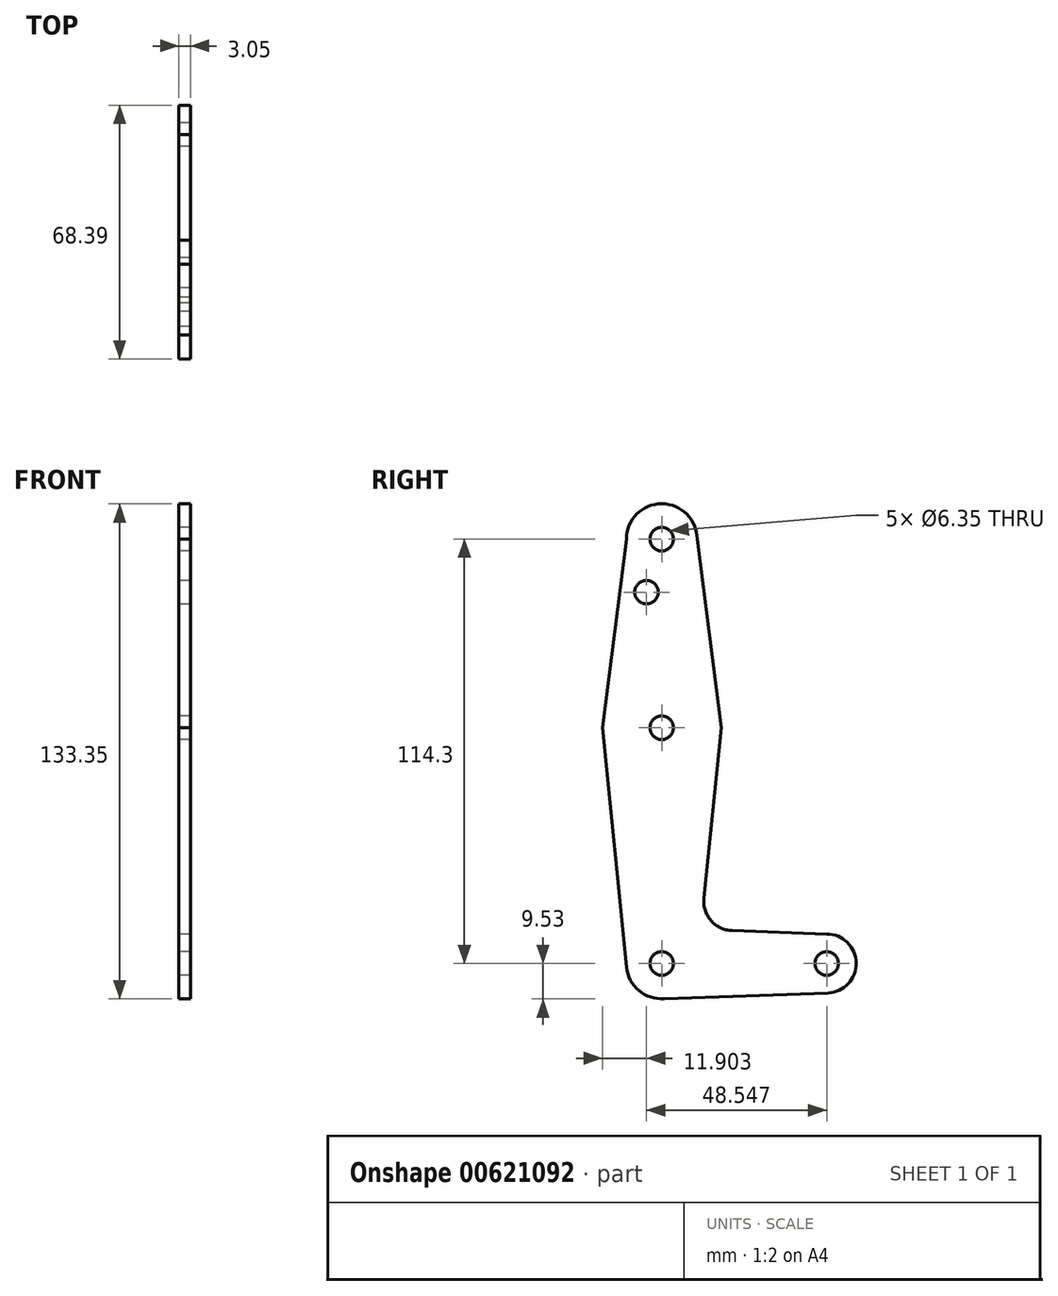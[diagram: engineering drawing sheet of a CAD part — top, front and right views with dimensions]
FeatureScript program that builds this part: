
annotation { "Feature Type Name" : "Feature", "Feature Type Description" : "" }
export const myFeature = defineFeature(function(context is Context, id is Id, definition is map)
    precondition{}
    {
        {
            var Q0;
            Q0=qCreatedBy(makeId("Right.planeOp"),FACE);
            var sketch = newSketch(context, id + "F0", { "sketchPlane" : qUnion([Q0])});
            skLineSegment(sketch, "E0", {"start": v(0, 0) * mm, "end": v(0, 50.8) * mm});
            skLineSegment(sketch, "E1", {"start": v(0, 50.8) * mm, "end": v(0, 0) * mm});
            skLineSegment(sketch, "E2", {"start": v(0, -63.5) * mm, "end": v(0, 0) * mm});
            skLineSegment(sketch, "E3", {"start": v(0, -63.5) * mm, "end": v(44.45, -63.5) * mm});
            skCircle(sketch, "E4", {"center": v(0, 0) * mm, "radius": 15.88 * mm});
            skCircle(sketch, "E5", {"center": v(0, 50.8) * mm, "radius": 9.53 * mm});
            skCircle(sketch, "E6", {"center": v(0, -63.5) * mm, "radius": 9.53 * mm});
            skCircle(sketch, "E7", {"center": v(44.45, -63.5) * mm, "radius": 7.94 * mm});
            skLineSegment(sketch, "E8", {"start": v(9.52, 50.8) * mm, "end": v(16, 0) * mm});
            skLineSegment(sketch, "E9", {"start": v(-9.52, 50.8) * mm, "end": v(-16, 0) * mm});
            skLineSegment(sketch, "E10", {"start": v(-16, 0) * mm, "end": v(-9.53, 50.8) * mm});
            skLineSegment(sketch, "E11", {"start": v(16, 0) * mm, "end": v(11.36, -45.9) * mm});
            skLineSegment(sketch, "E12", {"start": v(-16, 0) * mm, "end": v(-9.48, -64.46) * mm});
            skLineSegment(sketch, "E13", {"start": v(44.45, -55.56) * mm, "end": v(18.98, -54.65) * mm});
            skLineSegment(sketch, "E14", {"start": v(0, -73.03) * mm, "end": v(44.73, -71.43) * mm});
            skCircle(sketch, "E15", {"center": v(0, 50.8) * mm, "radius": 3.18 * mm});
            skArc(sketch, "E16.filletArc", {"start": v(11.36, -45.9) * mm, "mid": v(13.27, -51.93) * mm, "end": v(18.98, -54.65) * mm});
            skCircle(sketch, "E17", {"center": v(0, 0) * mm, "radius": 3.18 * mm});
            skCircle(sketch, "E18", {"center": v(0, -63.5) * mm, "radius": 3.18 * mm});
            skCircle(sketch, "E19", {"center": v(44.45, -63.5) * mm, "radius": 3.18 * mm});
            skCircle(sketch, "E20", {"center": v(-4.1, 36.53) * mm, "radius": 3.18 * mm});
            skSolve(sketch);
        }
        {
            var Q0;
            Q0 = qSketchRegion(id + "F0", true);
            var Q1;
            {var subQ0=sQuery(id+"F0.wireOp",EDGE,"E18");var subQ1=sQuery(id+"F0.wireOp",EDGE,"E2");var subQ2=makeQuery(id+"F0.imprint","INTERSECT",VERTEX,{"derivedFrom":[subQ1,subQ0]});Q1=makeQuery(id+"F0.imprint","IMPRINT",FACE,{"disambiguationData":[TD([[makeQuery(id+"F0.imprint","IMPRINT",EDGE,{"disambiguationData":[TD([[subQ2,-1.0]])],"derivedFrom":subQ1}),-1.0]])]});}
            extrude(context, id + "F1", {"entities" : qUnion([Q0, Q1]), "depth" : 3.05 * mm, "offsetDistance" : 25.4 * mm});
        }
    });
